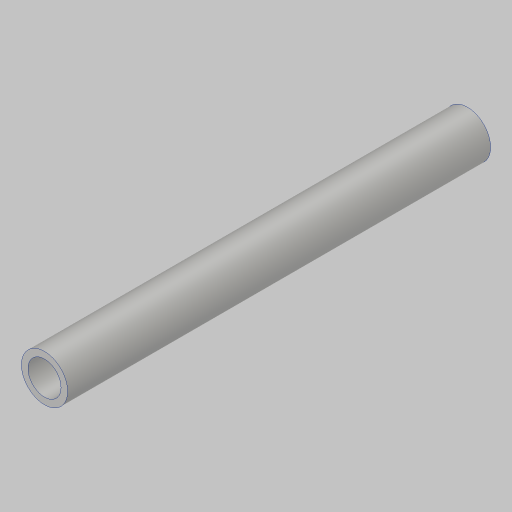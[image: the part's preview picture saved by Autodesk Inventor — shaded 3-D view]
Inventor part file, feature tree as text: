
AUTODESK INVENTOR PART (.ipt)
format: ipt  version: 2023.5 (Build 275446000, 446)  size: 92,160 bytes
history: native  units: in
note: dims shown in document units (in); Inventor stores cm internally (conversion verified against a paired STEP export)
features: extrude x1, sketch x1
ambient origin geometry x8: Origin, YZ Plane, XZ Plane, XY Plane, X Axis, Y Axis, Z Axis, Center Point
bodies: Solid1 (feature_tree)
feature tree (2):
  extrude  "Extrusion1"  Depth=8.0in
  sketch  "Sketch1"  dims[d0=0.875in d1=0.125in d2=8.0in d3=0.0in]
